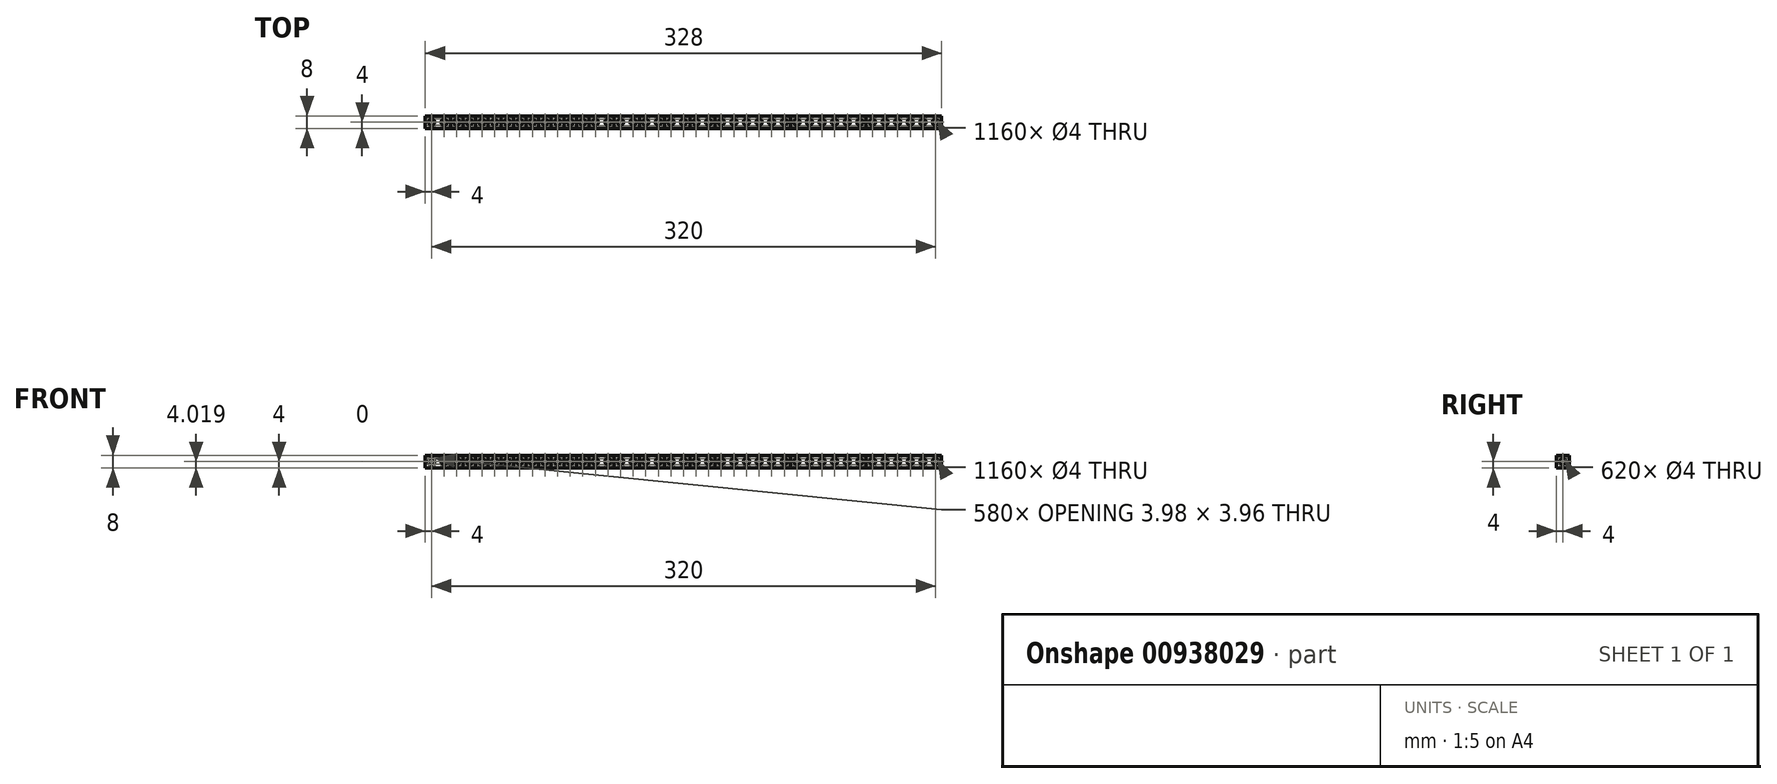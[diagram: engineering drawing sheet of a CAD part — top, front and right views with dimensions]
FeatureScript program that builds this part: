
annotation { "Feature Type Name" : "Feature", "Feature Type Description" : "" }
export const myFeature = defineFeature(function(context is Context, id is Id, definition is map)
    precondition{}
    {
        {
            var Q0;
            Q0=qCreatedBy(makeId("Right.planeOp"),FACE);
            var sketch = newSketch(context, id + "F0", { "sketchPlane" : qUnion([Q0]) });
            skLineSegment(sketch, "E0.bottom", {"start": v(4, 4) * mm, "end": v(-4, 4) * mm});
            skLineSegment(sketch, "E0.top", {"start": v(4, -4) * mm, "end": v(-4, -4) * mm});
            skLineSegment(sketch, "E0.left", {"start": v(4, 4) * mm, "end": v(4, -4) * mm});
            skLineSegment(sketch, "E0.right", {"start": v(-4, 4) * mm, "end": v(-4, -4) * mm});
            skPoint(sketch, "E0.middle", {"position": v(0, 0) * mm});
            skSolve(sketch);
        }
        {
            var Q0;
            Q0=qSketchRegion(id+"F0",true);
            extrude(context, id + "F1", {"entities" : qUnion([Q0]), "depth" : 16 * mm, "offsetDistance" : 25 * mm});
        }
        {
            var Q0;
            Q0=qSketchRegion(id+"F0",true);
            extrude(context, id + "F2", {"entities" : qUnion([Q0]), "depth" : 24 * mm, "offsetDistance" : 25 * mm});
        }
        {
            var Q0;
            Q0=qSketchRegion(id+"F0",true);
            extrude(context, id + "F3", {"entities" : qUnion([Q0]), "depth" : 32 * mm, "offsetDistance" : 25 * mm});
        }
        {
            var Q0;
            Q0=qSketchRegion(id+"F0",true);
            extrude(context, id + "F4", {"entities" : qUnion([Q0]), "depth" : 40 * mm, "offsetDistance" : 25 * mm});
        }
        {
            var Q0;
            Q0=qSketchRegion(id+"F0",true);
            extrude(context, id + "F5", {"entities" : qUnion([Q0]), "depth" : 48 * mm, "offsetDistance" : 25 * mm});
        }
        {
            var Q0;
            Q0=qSketchRegion(id+"F0",true);
            extrude(context, id + "F6", {"entities" : qUnion([Q0]), "depth" : 56 * mm, "offsetDistance" : 25 * mm});
        }
        {
            var Q0;
            Q0=qSketchRegion(id+"F0",true);
            extrude(context, id + "F7", {"entities" : qUnion([Q0]), "depth" : 64 * mm, "offsetDistance" : 25 * mm});
        }
        {
            var Q0;
            Q0=qSketchRegion(id+"F0",true);
            extrude(context, id + "F8", {"entities" : qUnion([Q0]), "depth" : 72 * mm, "offsetDistance" : 25 * mm});
        }
        {
            var Q0;
            Q0=qSketchRegion(id+"F0",true);
            extrude(context, id + "F9", {"entities" : qUnion([Q0]), "depth" : 80 * mm, "offsetDistance" : 25 * mm});
        }
        {
            var Q0;
            Q0=qSketchRegion(id+"F0",true);
            extrude(context, id + "F10", {"entities" : qUnion([Q0]), "depth" : 88 * mm, "offsetDistance" : 25 * mm});
        }
        {
            var Q0;
            Q0=qSketchRegion(id+"F0",true);
            extrude(context, id + "F11", {"entities" : qUnion([Q0]), "depth" : 96 * mm, "offsetDistance" : 25 * mm});
        }
        {
            var Q0;
            Q0=qSketchRegion(id+"F0",true);
            extrude(context, id + "F12", {"entities" : qUnion([Q0]), "depth" : 104 * mm, "offsetDistance" : 25 * mm});
        }
        {
            var Q0;
            Q0=qSketchRegion(id+"F0",true);
            extrude(context, id + "F13", {"entities" : qUnion([Q0]), "depth" : 120 * mm, "offsetDistance" : 25 * mm});
        }
        {
            var Q0;
            Q0=qSketchRegion(id+"F0",true);
            extrude(context, id + "F14", {"entities" : qUnion([Q0]), "depth" : 136 * mm, "offsetDistance" : 25 * mm});
        }
        {
            var Q0;
            Q0=qSketchRegion(id+"F0",true);
            extrude(context, id + "F15", {"entities" : qUnion([Q0]), "depth" : 152 * mm, "offsetDistance" : 25 * mm});
        }
        {
            var Q0;
            Q0=qSketchRegion(id+"F0",true);
            extrude(context, id + "F16", {"entities" : qUnion([Q0]), "depth" : 168 * mm, "offsetDistance" : 25 * mm});
        }
        {
            var Q0;
            Q0=qSketchRegion(id+"F0",true);
            extrude(context, id + "F17", {"entities" : qUnion([Q0]), "depth" : 184 * mm, "offsetDistance" : 25 * mm});
        }
        {
            var Q0;
            Q0=qSketchRegion(id+"F0",true);
            extrude(context, id + "F18", {"entities" : qUnion([Q0]), "depth" : 232 * mm, "offsetDistance" : 25 * mm});
        }
        {
            var Q0;
            Q0=qSketchRegion(id+"F0",true);
            extrude(context, id + "F19", {"entities" : qUnion([Q0]), "depth" : 280 * mm, "offsetDistance" : 25 * mm});
        }
        {
            var Q0;
            Q0=qSketchRegion(id+"F0",true);
            extrude(context, id + "F20", {"entities" : qUnion([Q0]), "depth" : 328 * mm, "offsetDistance" : 25 * mm});
        }
        {
            var Q0;
            Q0=qCreatedBy(makeId("Front.planeOp"),FACE);
            var sketch = newSketch(context, id + "F21", { "sketchPlane" : qUnion([Q0]) });
            skCircle(sketch, "E1", {"center": v(4, 0) * mm, "radius": 2 * mm});
            skCircle(sketch, "E2.1.0.0", {"center": v(12, 0) * mm, "radius": 2 * mm});
            skCircle(sketch, "E2.2.0.0", {"center": v(20, 0) * mm, "radius": 2 * mm});
            skCircle(sketch, "E2.3.0.0", {"center": v(28, 0) * mm, "radius": 2 * mm});
            skCircle(sketch, "E2.4.0.0", {"center": v(36, 0) * mm, "radius": 2 * mm});
            skCircle(sketch, "E2.5.0.0", {"center": v(44, 0) * mm, "radius": 2 * mm});
            skCircle(sketch, "E2.6.0.0", {"center": v(52, 0) * mm, "radius": 2 * mm});
            skCircle(sketch, "E2.7.0.0", {"center": v(60, 0) * mm, "radius": 2 * mm});
            skCircle(sketch, "E2.8.0.0", {"center": v(68, 0) * mm, "radius": 2 * mm});
            skCircle(sketch, "E2.9.0.0", {"center": v(76, 0) * mm, "radius": 2 * mm});
            skCircle(sketch, "E2.10.0.0", {"center": v(84, 0) * mm, "radius": 2 * mm});
            skCircle(sketch, "E2.11.0.0", {"center": v(92, 0) * mm, "radius": 2 * mm});
            skCircle(sketch, "E2.12.0.0", {"center": v(100, 0) * mm, "radius": 2 * mm});
            skCircle(sketch, "E2.13.0.0", {"center": v(108, 0) * mm, "radius": 2 * mm});
            skCircle(sketch, "E2.14.0.0", {"center": v(116, 0) * mm, "radius": 2 * mm});
            skCircle(sketch, "E2.15.0.0", {"center": v(124, 0) * mm, "radius": 2 * mm});
            skCircle(sketch, "E2.16.0.0", {"center": v(132, 0) * mm, "radius": 2 * mm});
            skCircle(sketch, "E2.17.0.0", {"center": v(140, 0) * mm, "radius": 2 * mm});
            skCircle(sketch, "E2.18.0.0", {"center": v(148, 0) * mm, "radius": 2 * mm});
            skCircle(sketch, "E2.19.0.0", {"center": v(156, 0) * mm, "radius": 2 * mm});
            skCircle(sketch, "E2.20.0.0", {"center": v(164, 0) * mm, "radius": 2 * mm});
            skCircle(sketch, "E2.21.0.0", {"center": v(172, 0) * mm, "radius": 2 * mm});
            skCircle(sketch, "E2.22.0.0", {"center": v(180, 0) * mm, "radius": 2 * mm});
            skCircle(sketch, "E2.23.0.0", {"center": v(188, 0) * mm, "radius": 2 * mm});
            skCircle(sketch, "E2.24.0.0", {"center": v(196, 0) * mm, "radius": 2 * mm});
            skCircle(sketch, "E2.25.0.0", {"center": v(204, 0) * mm, "radius": 2 * mm});
            skCircle(sketch, "E2.26.0.0", {"center": v(212, 0) * mm, "radius": 2 * mm});
            skCircle(sketch, "E2.27.0.0", {"center": v(220, 0) * mm, "radius": 2 * mm});
            skCircle(sketch, "E2.28.0.0", {"center": v(228, 0) * mm, "radius": 2 * mm});
            skCircle(sketch, "E2.29.0.0", {"center": v(236, 0) * mm, "radius": 2 * mm});
            skCircle(sketch, "E2.30.0.0", {"center": v(244, 0) * mm, "radius": 2 * mm});
            skCircle(sketch, "E2.31.0.0", {"center": v(252, 0) * mm, "radius": 2 * mm});
            skCircle(sketch, "E2.32.0.0", {"center": v(260, 0) * mm, "radius": 2 * mm});
            skCircle(sketch, "E2.33.0.0", {"center": v(268, 0) * mm, "radius": 2 * mm});
            skCircle(sketch, "E2.34.0.0", {"center": v(276, 0) * mm, "radius": 2 * mm});
            skCircle(sketch, "E2.35.0.0", {"center": v(284, 0) * mm, "radius": 2 * mm});
            skCircle(sketch, "E2.36.0.0", {"center": v(292, 0) * mm, "radius": 2 * mm});
            skCircle(sketch, "E2.37.0.0", {"center": v(300, 0) * mm, "radius": 2 * mm});
            skCircle(sketch, "E2.38.0.0", {"center": v(308, 0) * mm, "radius": 2 * mm});
            skCircle(sketch, "E2.39.0.0", {"center": v(316, 0) * mm, "radius": 2 * mm});
            skCircle(sketch, "E2.40.0.0", {"center": v(324, 0) * mm, "radius": 2 * mm});
            skLineSegment(sketch, "E2.direction1", {"start": v(4, 0) * mm, "end": v(12, 0) * mm, "construction": true});
            skSolve(sketch);
        }
        {
            var Q0;
            Q0=qSketchRegion(id+"F21",true);
            extrude(context, id + "F22", {"entities" : qUnion([Q0]), "operationType" : NewBodyOperationType.REMOVE, "endBound" : BoundingType.SYMMETRIC, "oppositeDirection" : true, "depth" : 25 * mm, "offsetDistance" : 25 * mm});
        }
        {
            var Q0;
            Q0=qCreatedBy(makeId("Top.planeOp"),FACE);
            var sketch = newSketch(context, id + "F23", { "sketchPlane" : qUnion([Q0]) });
            skCircle(sketch, "E3", {"center": v(4, 0) * mm, "radius": 2 * mm});
            skCircle(sketch, "E4.1.0.0", {"center": v(12, 0) * mm, "radius": 2 * mm});
            skCircle(sketch, "E4.2.0.0", {"center": v(20, 0) * mm, "radius": 2 * mm});
            skCircle(sketch, "E4.3.0.0", {"center": v(28, 0) * mm, "radius": 2 * mm});
            skCircle(sketch, "E4.4.0.0", {"center": v(36, 0) * mm, "radius": 2 * mm});
            skCircle(sketch, "E4.5.0.0", {"center": v(44, 0) * mm, "radius": 2 * mm});
            skCircle(sketch, "E4.6.0.0", {"center": v(52, 0) * mm, "radius": 2 * mm});
            skCircle(sketch, "E4.7.0.0", {"center": v(60, 0) * mm, "radius": 2 * mm});
            skCircle(sketch, "E4.8.0.0", {"center": v(68, 0) * mm, "radius": 2 * mm});
            skCircle(sketch, "E4.9.0.0", {"center": v(76, 0) * mm, "radius": 2 * mm});
            skCircle(sketch, "E4.10.0.0", {"center": v(84, 0) * mm, "radius": 2 * mm});
            skCircle(sketch, "E4.11.0.0", {"center": v(92, 0) * mm, "radius": 2 * mm});
            skCircle(sketch, "E4.12.0.0", {"center": v(100, 0) * mm, "radius": 2 * mm});
            skCircle(sketch, "E4.13.0.0", {"center": v(108, 0) * mm, "radius": 2 * mm});
            skCircle(sketch, "E4.14.0.0", {"center": v(116, 0) * mm, "radius": 2 * mm});
            skCircle(sketch, "E4.15.0.0", {"center": v(124, 0) * mm, "radius": 2 * mm});
            skCircle(sketch, "E4.16.0.0", {"center": v(132, 0) * mm, "radius": 2 * mm});
            skCircle(sketch, "E4.17.0.0", {"center": v(140, 0) * mm, "radius": 2 * mm});
            skCircle(sketch, "E4.18.0.0", {"center": v(148, 0) * mm, "radius": 2 * mm});
            skCircle(sketch, "E4.19.0.0", {"center": v(156, 0) * mm, "radius": 2 * mm});
            skCircle(sketch, "E4.20.0.0", {"center": v(164, 0) * mm, "radius": 2 * mm});
            skCircle(sketch, "E4.21.0.0", {"center": v(172, 0) * mm, "radius": 2 * mm});
            skCircle(sketch, "E4.22.0.0", {"center": v(180, 0) * mm, "radius": 2 * mm});
            skCircle(sketch, "E4.23.0.0", {"center": v(188, 0) * mm, "radius": 2 * mm});
            skCircle(sketch, "E4.24.0.0", {"center": v(196, 0) * mm, "radius": 2 * mm});
            skCircle(sketch, "E4.25.0.0", {"center": v(204, 0) * mm, "radius": 2 * mm});
            skCircle(sketch, "E4.26.0.0", {"center": v(212, 0) * mm, "radius": 2 * mm});
            skCircle(sketch, "E4.27.0.0", {"center": v(220, 0) * mm, "radius": 2 * mm});
            skCircle(sketch, "E4.28.0.0", {"center": v(228, 0) * mm, "radius": 2 * mm});
            skCircle(sketch, "E4.29.0.0", {"center": v(236, 0) * mm, "radius": 2 * mm});
            skCircle(sketch, "E4.30.0.0", {"center": v(244, 0) * mm, "radius": 2 * mm});
            skCircle(sketch, "E4.31.0.0", {"center": v(252, 0) * mm, "radius": 2 * mm});
            skCircle(sketch, "E4.32.0.0", {"center": v(260, 0) * mm, "radius": 2 * mm});
            skCircle(sketch, "E4.33.0.0", {"center": v(268, 0) * mm, "radius": 2 * mm});
            skCircle(sketch, "E4.34.0.0", {"center": v(276, 0) * mm, "radius": 2 * mm});
            skCircle(sketch, "E4.35.0.0", {"center": v(284, 0) * mm, "radius": 2 * mm});
            skCircle(sketch, "E4.36.0.0", {"center": v(292, 0) * mm, "radius": 2 * mm});
            skCircle(sketch, "E4.37.0.0", {"center": v(300, 0) * mm, "radius": 2 * mm});
            skCircle(sketch, "E4.38.0.0", {"center": v(308, 0) * mm, "radius": 2 * mm});
            skCircle(sketch, "E4.39.0.0", {"center": v(316, 0) * mm, "radius": 2 * mm});
            skCircle(sketch, "E4.40.0.0", {"center": v(324, 0) * mm, "radius": 2 * mm});
            skLineSegment(sketch, "E4.direction1", {"start": v(4, 0) * mm, "end": v(12, 0) * mm, "construction": true});
            skSolve(sketch);
        }
        {
            var Q0;
            Q0=qSketchRegion(id+"F23",true);
            extrude(context, id + "F24", {"entities" : qUnion([Q0]), "operationType" : NewBodyOperationType.REMOVE, "endBound" : BoundingType.SYMMETRIC, "depth" : 25 * mm, "offsetDistance" : 25 * mm});
        }
        {
            var Q0;
            Q0=qCreatedBy(makeId("Right.planeOp"),FACE);
            var sketch = newSketch(context, id + "F25", { "sketchPlane" : qUnion([Q0]) });
            skCircle(sketch, "E5", {"center": v(0, 0) * mm, "radius": 2 * mm});
            skSolve(sketch);
        }
        {
            var Q0;
            Q0=qSketchRegion(id+"F25",true);
            extrude(context, id + "F26", {"entities" : qUnion([Q0]), "operationType" : NewBodyOperationType.REMOVE, "depth" : 12 * mm, "offsetDistance" : 25 * mm});
        }
        {
            var Q0;
            Q0=qCreatedBy(makeId("Right.planeOp"),FACE);
            cPlane(context, id + "F27", {"entities" : qUnion([Q0]), "cplaneType" : CPlaneType.OFFSET, "offset" : 328 * mm, "width" : 150 * mm, "height" : 150 * mm});
        }
        {
            var Q0;
            Q0=qCreatedBy(id+"F27.planeOp",FACE);
            var sketch = newSketch(context, id + "F28", { "sketchPlane" : qUnion([Q0]) });
            skCircle(sketch, "E6", {"center": v(0, 0) * mm, "radius": 2 * mm});
            skSolve(sketch);
        }
        {
            var Q0;
            Q0=qSketchRegion(id+"F28",true);
            var Q1;
            {var subQ0=makeQuery(id+"F24.opExtrude","SWEPT_FACE",FACE,{"disambiguationData":[OSD([sQuery(id+"F23.wireOp",EDGE,"E4.1.0.0")])]});Q1=makeQuery(id+"F24.boolean.opBoolean","COPY",FACE,{"disambiguationData":[TD([makeQuery(id+"F1.opExtrude","SWEPT_FACE",FACE,{"disambiguationData":[OSD([sQuery(id+"F0.wireOp",EDGE,"E0.top")])]})])],"derivedFrom":subQ0});}
            extrude(context, id + "F29", {"entities" : qUnion([Q0]), "operationType" : NewBodyOperationType.REMOVE, "endBound" : BoundingType.UP_TO_SURFACE, "oppositeDirection" : true, "depth" : 25 * mm, "endBoundEntityFace" : qUnion([Q1]), "offsetDistance" : 25 * mm});
        }
        {
            var Q0;
            Q0=qSketchRegion(id+"F28",true);
            var Q1;
            {var subQ0=makeQuery(id+"F24.opExtrude","SWEPT_FACE",FACE,{"disambiguationData":[OSD([sQuery(id+"F23.wireOp",EDGE,"E4.1.0.0")])]});Q1=makeQuery(id+"F24.boolean.opBoolean","COPY",FACE,{"disambiguationData":[TD([makeQuery(id+"F1.opExtrude","SWEPT_FACE",FACE,{"disambiguationData":[OSD([sQuery(id+"F0.wireOp",EDGE,"E0.top")])]})])],"derivedFrom":subQ0});}
            extrude(context, id + "F30", {"entities" : qUnion([Q0]), "operationType" : NewBodyOperationType.REMOVE, "endBound" : BoundingType.UP_TO_SURFACE, "oppositeDirection" : true, "depth" : 25 * mm, "endBoundEntityFace" : qUnion([Q1]), "offsetDistance" : 25 * mm});
        }
        {
            var Q0;
            Q0=qSketchRegion(id+"F28",true);
            var Q1;
            {var subQ0=makeQuery(id+"F24.opExtrude","SWEPT_FACE",FACE,{"disambiguationData":[OSD([sQuery(id+"F23.wireOp",EDGE,"E4.2.0.0")])]});Q1=makeQuery(id+"F24.boolean.opBoolean","COPY",FACE,{"disambiguationData":[TD([makeQuery(id+"F2.opExtrude","SWEPT_FACE",FACE,{"disambiguationData":[OSD([sQuery(id+"F0.wireOp",EDGE,"E0.top")])]})])],"derivedFrom":subQ0});}
            extrude(context, id + "F31", {"entities" : qUnion([Q0]), "operationType" : NewBodyOperationType.REMOVE, "endBound" : BoundingType.UP_TO_SURFACE, "oppositeDirection" : true, "depth" : 25 * mm, "endBoundEntityFace" : qUnion([Q1]), "offsetDistance" : 25 * mm});
        }
        {
            var Q0;
            Q0=qSketchRegion(id+"F28",true);
            var Q1;
            {var subQ0=makeQuery(id+"F24.opExtrude","SWEPT_FACE",FACE,{"disambiguationData":[OSD([sQuery(id+"F23.wireOp",EDGE,"E4.3.0.0")])]});Q1=makeQuery(id+"F24.boolean.opBoolean","COPY",FACE,{"disambiguationData":[TD([makeQuery(id+"F3.opExtrude","SWEPT_FACE",FACE,{"disambiguationData":[OSD([sQuery(id+"F0.wireOp",EDGE,"E0.top")])]})])],"derivedFrom":subQ0});}
            extrude(context, id + "F32", {"entities" : qUnion([Q0]), "operationType" : NewBodyOperationType.REMOVE, "endBound" : BoundingType.UP_TO_SURFACE, "oppositeDirection" : true, "depth" : 25 * mm, "endBoundEntityFace" : qUnion([Q1]), "offsetDistance" : 25 * mm});
        }
        {
            var Q0;
            Q0=qSketchRegion(id+"F28",true);
            var Q1;
            {var subQ0=makeQuery(id+"F24.opExtrude","SWEPT_FACE",FACE,{"disambiguationData":[OSD([sQuery(id+"F23.wireOp",EDGE,"E4.4.0.0")])]});Q1=makeQuery(id+"F24.boolean.opBoolean","COPY",FACE,{"disambiguationData":[TD([makeQuery(id+"F5.opExtrude","SWEPT_FACE",FACE,{"disambiguationData":[OSD([sQuery(id+"F0.wireOp",EDGE,"E0.top")])]})])],"derivedFrom":subQ0});}
            extrude(context, id + "F33", {"entities" : qUnion([Q0]), "operationType" : NewBodyOperationType.REMOVE, "endBound" : BoundingType.UP_TO_SURFACE, "oppositeDirection" : true, "depth" : 25 * mm, "endBoundEntityFace" : qUnion([Q1]), "offsetDistance" : 25 * mm});
        }
        {
            var Q0;
            Q0=qSketchRegion(id+"F28",true);
            var Q1;
            {var subQ0=makeQuery(id+"F24.opExtrude","SWEPT_FACE",FACE,{"disambiguationData":[OSD([sQuery(id+"F23.wireOp",EDGE,"E4.5.0.0")])]});Q1=makeQuery(id+"F24.boolean.opBoolean","COPY",FACE,{"disambiguationData":[TD([makeQuery(id+"F6.opExtrude","SWEPT_FACE",FACE,{"disambiguationData":[OSD([sQuery(id+"F0.wireOp",EDGE,"E0.top")])]})])],"derivedFrom":subQ0});}
            extrude(context, id + "F34", {"entities" : qUnion([Q0]), "operationType" : NewBodyOperationType.REMOVE, "endBound" : BoundingType.UP_TO_SURFACE, "oppositeDirection" : true, "depth" : 25 * mm, "endBoundEntityFace" : qUnion([Q1]), "offsetDistance" : 25 * mm});
        }
        {
            var Q0;
            Q0=qSketchRegion(id+"F28",true);
            var Q1;
            {var subQ0=makeQuery(id+"F24.opExtrude","SWEPT_FACE",FACE,{"disambiguationData":[OSD([sQuery(id+"F23.wireOp",EDGE,"E4.6.0.0")])]});Q1=makeQuery(id+"F24.boolean.opBoolean","COPY",FACE,{"disambiguationData":[TD([makeQuery(id+"F7.opExtrude","SWEPT_FACE",FACE,{"disambiguationData":[OSD([sQuery(id+"F0.wireOp",EDGE,"E0.top")])]})])],"derivedFrom":subQ0});}
            extrude(context, id + "F35", {"entities" : qUnion([Q0]), "operationType" : NewBodyOperationType.REMOVE, "endBound" : BoundingType.UP_TO_SURFACE, "oppositeDirection" : true, "depth" : 25 * mm, "endBoundEntityFace" : qUnion([Q1]), "offsetDistance" : 25 * mm});
        }
        {
            var Q0;
            Q0=qSketchRegion(id+"F28",true);
            var Q1;
            {var subQ0=makeQuery(id+"F24.opExtrude","SWEPT_FACE",FACE,{"disambiguationData":[OSD([sQuery(id+"F23.wireOp",EDGE,"E4.7.0.0")])]});Q1=makeQuery(id+"F24.boolean.opBoolean","COPY",FACE,{"disambiguationData":[TD([makeQuery(id+"F8.opExtrude","SWEPT_FACE",FACE,{"disambiguationData":[OSD([sQuery(id+"F0.wireOp",EDGE,"E0.top")])]})])],"derivedFrom":subQ0});}
            extrude(context, id + "F36", {"entities" : qUnion([Q0]), "operationType" : NewBodyOperationType.REMOVE, "endBound" : BoundingType.UP_TO_SURFACE, "oppositeDirection" : true, "depth" : 25 * mm, "endBoundEntityFace" : qUnion([Q1]), "offsetDistance" : 25 * mm});
        }
        {
            var Q0;
            Q0=qSketchRegion(id+"F28",true);
            var Q1;
            {var subQ0=makeQuery(id+"F24.opExtrude","SWEPT_FACE",FACE,{"disambiguationData":[OSD([sQuery(id+"F23.wireOp",EDGE,"E4.8.0.0")])]});Q1=makeQuery(id+"F24.boolean.opBoolean","COPY",FACE,{"disambiguationData":[TD([makeQuery(id+"F9.opExtrude","SWEPT_FACE",FACE,{"disambiguationData":[OSD([sQuery(id+"F0.wireOp",EDGE,"E0.top")])]})])],"derivedFrom":subQ0});}
            extrude(context, id + "F37", {"entities" : qUnion([Q0]), "operationType" : NewBodyOperationType.REMOVE, "endBound" : BoundingType.UP_TO_SURFACE, "oppositeDirection" : true, "depth" : 25 * mm, "endBoundEntityFace" : qUnion([Q1]), "offsetDistance" : 25 * mm});
        }
        {
            var Q0;
            Q0=qSketchRegion(id+"F28",true);
            var Q1;
            {var subQ0=makeQuery(id+"F24.opExtrude","SWEPT_FACE",FACE,{"disambiguationData":[OSD([sQuery(id+"F23.wireOp",EDGE,"E4.9.0.0")])]});Q1=makeQuery(id+"F24.boolean.opBoolean","COPY",FACE,{"disambiguationData":[TD([makeQuery(id+"F10.opExtrude","SWEPT_FACE",FACE,{"disambiguationData":[OSD([sQuery(id+"F0.wireOp",EDGE,"E0.top")])]})])],"derivedFrom":subQ0});}
            extrude(context, id + "F38", {"entities" : qUnion([Q0]), "operationType" : NewBodyOperationType.REMOVE, "endBound" : BoundingType.UP_TO_SURFACE, "oppositeDirection" : true, "depth" : 25 * mm, "endBoundEntityFace" : qUnion([Q1]), "offsetDistance" : 25 * mm});
        }
        {
            var Q0;
            Q0=qSketchRegion(id+"F28",true);
            var Q1;
            {var subQ0=makeQuery(id+"F24.opExtrude","SWEPT_FACE",FACE,{"disambiguationData":[OSD([sQuery(id+"F23.wireOp",EDGE,"E4.10.0.0")])]});Q1=makeQuery(id+"F24.boolean.opBoolean","COPY",FACE,{"disambiguationData":[TD([makeQuery(id+"F11.opExtrude","SWEPT_FACE",FACE,{"disambiguationData":[OSD([sQuery(id+"F0.wireOp",EDGE,"E0.top")])]})])],"derivedFrom":subQ0});}
            extrude(context, id + "F39", {"entities" : qUnion([Q0]), "operationType" : NewBodyOperationType.REMOVE, "endBound" : BoundingType.UP_TO_SURFACE, "oppositeDirection" : true, "depth" : 25 * mm, "endBoundEntityFace" : qUnion([Q1]), "offsetDistance" : 25 * mm});
        }
        {
            var Q0;
            Q0=qSketchRegion(id+"F28",true);
            var Q1;
            {var subQ0=makeQuery(id+"F24.opExtrude","SWEPT_FACE",FACE,{"disambiguationData":[OSD([sQuery(id+"F23.wireOp",EDGE,"E4.11.0.0")])]});Q1=makeQuery(id+"F24.boolean.opBoolean","COPY",FACE,{"disambiguationData":[TD([makeQuery(id+"F12.opExtrude","SWEPT_FACE",FACE,{"disambiguationData":[OSD([sQuery(id+"F0.wireOp",EDGE,"E0.top")])]})])],"derivedFrom":subQ0});}
            extrude(context, id + "F40", {"entities" : qUnion([Q0]), "operationType" : NewBodyOperationType.REMOVE, "endBound" : BoundingType.UP_TO_SURFACE, "oppositeDirection" : true, "depth" : 25 * mm, "endBoundEntityFace" : qUnion([Q1]), "offsetDistance" : 25 * mm});
        }
        {
            var Q0;
            Q0=qSketchRegion(id+"F28",true);
            var Q1;
            {var subQ0=makeQuery(id+"F24.opExtrude","SWEPT_FACE",FACE,{"disambiguationData":[OSD([sQuery(id+"F23.wireOp",EDGE,"E4.13.0.0")])]});Q1=makeQuery(id+"F24.boolean.opBoolean","COPY",FACE,{"disambiguationData":[TD([makeQuery(id+"F13.opExtrude","SWEPT_FACE",FACE,{"disambiguationData":[OSD([sQuery(id+"F0.wireOp",EDGE,"E0.top")])]})])],"derivedFrom":subQ0});}
            extrude(context, id + "F41", {"entities" : qUnion([Q0]), "operationType" : NewBodyOperationType.REMOVE, "endBound" : BoundingType.UP_TO_SURFACE, "oppositeDirection" : true, "depth" : 25 * mm, "endBoundEntityFace" : qUnion([Q1]), "offsetDistance" : 25 * mm});
        }
        {
            var Q0;
            Q0=qSketchRegion(id+"F28",true);
            var Q1;
            {var subQ0=makeQuery(id+"F24.opExtrude","SWEPT_FACE",FACE,{"disambiguationData":[OSD([sQuery(id+"F23.wireOp",EDGE,"E4.15.0.0")])]});Q1=makeQuery(id+"F24.boolean.opBoolean","COPY",FACE,{"disambiguationData":[TD([makeQuery(id+"F14.opExtrude","SWEPT_FACE",FACE,{"disambiguationData":[OSD([sQuery(id+"F0.wireOp",EDGE,"E0.top")])]})])],"derivedFrom":subQ0});}
            extrude(context, id + "F42", {"entities" : qUnion([Q0]), "operationType" : NewBodyOperationType.REMOVE, "endBound" : BoundingType.UP_TO_SURFACE, "oppositeDirection" : true, "depth" : 25 * mm, "endBoundEntityFace" : qUnion([Q1]), "offsetDistance" : 25 * mm});
        }
        {
            var Q0;
            Q0=qSketchRegion(id+"F28",true);
            var Q1;
            {var subQ0=makeQuery(id+"F24.opExtrude","SWEPT_FACE",FACE,{"disambiguationData":[OSD([sQuery(id+"F23.wireOp",EDGE,"E4.17.0.0")])]});Q1=makeQuery(id+"F24.boolean.opBoolean","COPY",FACE,{"disambiguationData":[TD([makeQuery(id+"F15.opExtrude","SWEPT_FACE",FACE,{"disambiguationData":[OSD([sQuery(id+"F0.wireOp",EDGE,"E0.top")])]})])],"derivedFrom":subQ0});}
            extrude(context, id + "F43", {"entities" : qUnion([Q0]), "operationType" : NewBodyOperationType.REMOVE, "endBound" : BoundingType.UP_TO_SURFACE, "oppositeDirection" : true, "depth" : 25 * mm, "endBoundEntityFace" : qUnion([Q1]), "offsetDistance" : 25 * mm});
        }
        {
            var Q0;
            Q0=qSketchRegion(id+"F28",true);
            var Q1;
            {var subQ0=makeQuery(id+"F24.opExtrude","SWEPT_FACE",FACE,{"disambiguationData":[OSD([sQuery(id+"F23.wireOp",EDGE,"E4.19.0.0")])]});Q1=makeQuery(id+"F24.boolean.opBoolean","COPY",FACE,{"disambiguationData":[TD([makeQuery(id+"F16.opExtrude","SWEPT_FACE",FACE,{"disambiguationData":[OSD([sQuery(id+"F0.wireOp",EDGE,"E0.top")])]})])],"derivedFrom":subQ0});}
            extrude(context, id + "F44", {"entities" : qUnion([Q0]), "operationType" : NewBodyOperationType.REMOVE, "endBound" : BoundingType.UP_TO_SURFACE, "oppositeDirection" : true, "depth" : 25 * mm, "endBoundEntityFace" : qUnion([Q1]), "offsetDistance" : 25 * mm});
        }
        {
            var Q0;
            Q0=qSketchRegion(id+"F28",true);
            var Q1;
            {var subQ0=makeQuery(id+"F24.opExtrude","SWEPT_FACE",FACE,{"disambiguationData":[OSD([sQuery(id+"F23.wireOp",EDGE,"E4.21.0.0")])]});Q1=makeQuery(id+"F24.boolean.opBoolean","COPY",FACE,{"disambiguationData":[TD([makeQuery(id+"F17.opExtrude","SWEPT_FACE",FACE,{"disambiguationData":[OSD([sQuery(id+"F0.wireOp",EDGE,"E0.top")])]})])],"derivedFrom":subQ0});}
            extrude(context, id + "F45", {"entities" : qUnion([Q0]), "operationType" : NewBodyOperationType.REMOVE, "endBound" : BoundingType.UP_TO_SURFACE, "oppositeDirection" : true, "depth" : 25 * mm, "endBoundEntityFace" : qUnion([Q1]), "offsetDistance" : 25 * mm});
        }
        {
            var Q0;
            Q0=qSketchRegion(id+"F28",true);
            var Q1;
            {var subQ0=makeQuery(id+"F24.opExtrude","SWEPT_FACE",FACE,{"disambiguationData":[OSD([sQuery(id+"F23.wireOp",EDGE,"E4.27.0.0")])]});Q1=makeQuery(id+"F24.boolean.opBoolean","COPY",FACE,{"disambiguationData":[TD([makeQuery(id+"F18.opExtrude","SWEPT_FACE",FACE,{"disambiguationData":[OSD([sQuery(id+"F0.wireOp",EDGE,"E0.top")])]})])],"derivedFrom":subQ0});}
            extrude(context, id + "F46", {"entities" : qUnion([Q0]), "operationType" : NewBodyOperationType.REMOVE, "endBound" : BoundingType.UP_TO_SURFACE, "oppositeDirection" : true, "depth" : 25 * mm, "endBoundEntityFace" : qUnion([Q1]), "offsetDistance" : 25 * mm});
        }
        {
            var Q0;
            Q0=qSketchRegion(id+"F28",true);
            var Q1;
            {var subQ0=makeQuery(id+"F24.opExtrude","SWEPT_FACE",FACE,{"disambiguationData":[OSD([sQuery(id+"F23.wireOp",EDGE,"E4.33.0.0")])]});Q1=makeQuery(id+"F24.boolean.opBoolean","COPY",FACE,{"disambiguationData":[TD([makeQuery(id+"F19.opExtrude","SWEPT_FACE",FACE,{"disambiguationData":[OSD([sQuery(id+"F0.wireOp",EDGE,"E0.top")])]})])],"derivedFrom":subQ0});}
            extrude(context, id + "F47", {"entities" : qUnion([Q0]), "operationType" : NewBodyOperationType.REMOVE, "endBound" : BoundingType.UP_TO_SURFACE, "oppositeDirection" : true, "depth" : 25 * mm, "endBoundEntityFace" : qUnion([Q1]), "offsetDistance" : 25 * mm});
        }
        {
            var Q0;
            Q0=qSketchRegion(id+"F28",true);
            var Q1;
            {var subQ0=makeQuery(id+"F24.opExtrude","SWEPT_FACE",FACE,{"disambiguationData":[OSD([sQuery(id+"F23.wireOp",EDGE,"E4.39.0.0")])]});Q1=makeQuery(id+"F24.boolean.opBoolean","COPY",FACE,{"disambiguationData":[TD([makeQuery(id+"F20.opExtrude","SWEPT_FACE",FACE,{"disambiguationData":[OSD([sQuery(id+"F0.wireOp",EDGE,"E0.top")])]})])],"derivedFrom":subQ0});}
            extrude(context, id + "F48", {"entities" : qUnion([Q0]), "operationType" : NewBodyOperationType.REMOVE, "endBound" : BoundingType.UP_TO_SURFACE, "oppositeDirection" : true, "depth" : 25 * mm, "endBoundEntityFace" : qUnion([Q1]), "offsetDistance" : 25 * mm});
        }
    });
